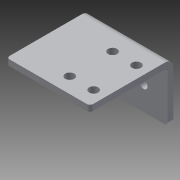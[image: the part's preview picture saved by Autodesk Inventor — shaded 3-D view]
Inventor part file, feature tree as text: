
AUTODESK INVENTOR PART (.ipt)
format: ipt  version: 2014 (Build 180170000, 170)  size: 136,192 bytes
history: native  units: in
note: dims shown in document units (in); Inventor stores cm internally (conversion verified against a paired STEP export)
features: sheet_metal_op x4, sketch x3, other x2, fillet x1, extrude x1
ambient origin geometry x8: Origin, YZ Plane, XZ Plane, XY Plane, X Axis, Y Axis, Z Axis, Center Point
bodies: Solid1 (feature_tree)
feature tree (11):
  sheet_metal_op  "Face1"
  sheet_metal_op  "Flange1"
  fillet  "Fillet1"  Radius=1.75in
  extrude  "Extrusion1"  Depth=0.163in
  sketch  "Sketch1"  dims[d1=1.0in d2=0.163in]
  other  "Plate1"
  sketch  "Sketch2"  dims[d3=0.25in]
  other  "Plate2"
  sheet_metal_op  "Bend1"
  sheet_metal_op  "Corner1"
  sketch  "Sketch3"  dims[d4=0.7874in d6=1.0in d7=0.3937in d9=1.0in d11=0.125in d12=0.125in d13=0.0625in d14=0.25in d15=0.125in d16=1.75in d17=90.0deg d18=0.05in d19=0.5in d20=0.125in d21=0.125in d22=0.0625in d23=1.35in d24=0.75in d25=0.125in d26=0.875in d27=0.19in d28=0.125in d29=0.2265in d30=1.0in d31=0.0in]
